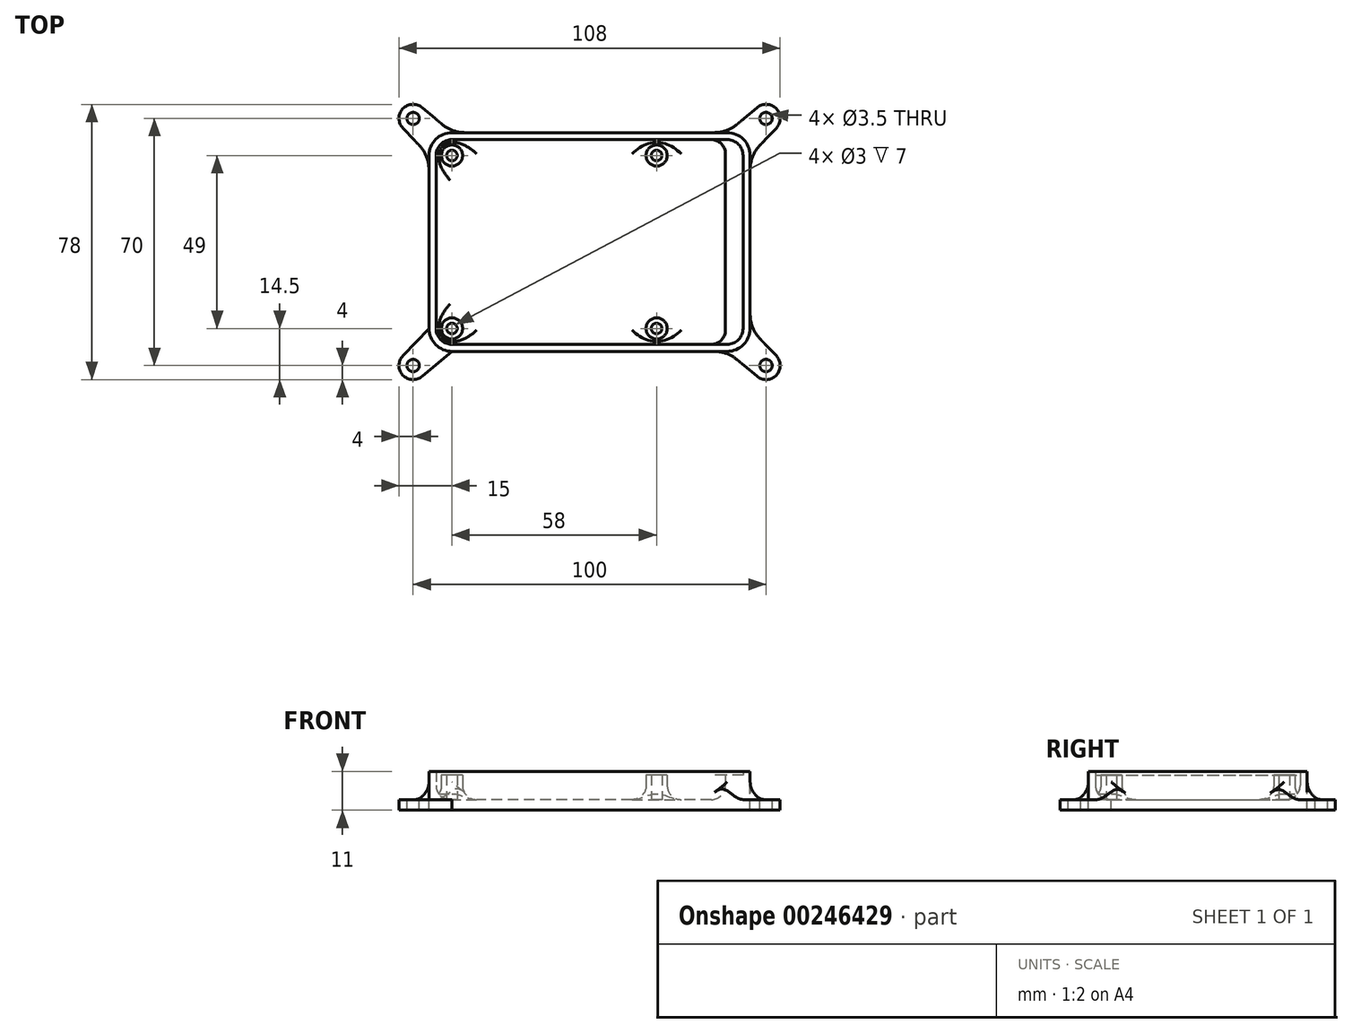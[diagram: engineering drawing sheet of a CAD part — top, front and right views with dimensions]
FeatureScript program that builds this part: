
annotation { "Feature Type Name" : "Feature", "Feature Type Description" : "" }
export const myFeature = defineFeature(function(context is Context, id is Id, definition is map)
    precondition{}
    {
        {
            var Q0;
            Q0=qCreatedBy(makeId("Top.planeOp"),FACE);
            var sketch = newSketch(context, id + "F0", { "sketchPlane" : qUnion([Q0])});
            skLineSegment(sketch, "E0.bottom", {"start": v(3.5, 0) * mm, "end": v(81.5, 0) * mm});
            skLineSegment(sketch, "E0.top", {"start": v(3.5, 56) * mm, "end": v(81.5, 56) * mm});
            skLineSegment(sketch, "E0.left", {"start": v(0, 3.5) * mm, "end": v(0, 52.5) * mm});
            skLineSegment(sketch, "E0.right", {"start": v(85, 3.5) * mm, "end": v(85, 52.5) * mm});
            skPoint(sketch, "E1.visualSharp", {"position": v(0, 56) * mm});
            skArc(sketch, "E1.filletArc", {"start": v(3.5, 56) * mm, "mid": v(1.03, 54.97) * mm, "end": v(0, 52.5) * mm});
            skPoint(sketch, "E2.visualSharp", {"position": v(85, 56) * mm});
            skArc(sketch, "E2.filletArc", {"start": v(85, 52.5) * mm, "mid": v(83.97, 54.97) * mm, "end": v(81.5, 56) * mm});
            skPoint(sketch, "E3.visualSharp", {"position": v(85, 0) * mm});
            skArc(sketch, "E3.filletArc", {"start": v(81.5, 0) * mm, "mid": v(83.97, 1.03) * mm, "end": v(85, 3.5) * mm});
            skPoint(sketch, "E4.visualSharp", {"position": v(0, 0) * mm});
            skArc(sketch, "E4.filletArc", {"start": v(0, 3.5) * mm, "mid": v(1.03, 1.03) * mm, "end": v(3.5, 0) * mm});
            skSolve(sketch);
        }
        {
            var Q0;
            Q0=makeQuery(id+"F0.imprint","IMPRINT",FACE,{"disambiguationData":[TD([[makeQuery(id+"F0.imprint","IMPRINT",EDGE,{"derivedFrom":sQuery(id+"F0.wireOp",EDGE,"E0.bottom")}),1.0]])]});
            var sketch = newSketch(context, id + "F1", { "sketchPlane" : qUnion([Q0])});
            skLineSegment(sketch, "E5.0.0", {"start": v(81.5, 56) * mm, "end": v(3.5, 56) * mm});
            skArc(sketch, "E5.0.1", {"start": v(3.5, 56) * mm, "mid": v(1.03, 54.97) * mm, "end": v(0, 52.5) * mm});
            skLineSegment(sketch, "E5.0.2", {"start": v(0, 52.5) * mm, "end": v(0, 3.5) * mm});
            skArc(sketch, "E5.0.3", {"start": v(0, 3.5) * mm, "mid": v(1.03, 1.03) * mm, "end": v(3.5, 0) * mm});
            skLineSegment(sketch, "E5.0.4", {"start": v(3.5, 0) * mm, "end": v(81.5, 0) * mm});
            skArc(sketch, "E5.0.5", {"start": v(81.5, 0) * mm, "mid": v(83.97, 1.03) * mm, "end": v(85, 3.5) * mm});
            skLineSegment(sketch, "E5.0.6", {"start": v(85, 3.5) * mm, "end": v(85, 52.5) * mm});
            skArc(sketch, "E5.0.7", {"start": v(85, 52.5) * mm, "mid": v(83.97, 54.97) * mm, "end": v(81.5, 56) * mm});
            skLineSegment(sketch, "E6.bottom", {"start": v(81.5, -1) * mm, "end": v(3.5, -1) * mm});
            skLineSegment(sketch, "E6.top", {"start": v(81.5, 57) * mm, "end": v(3.5, 57) * mm});
            skLineSegment(sketch, "E6.left", {"start": v(86, 3.5) * mm, "end": v(86, 52.5) * mm});
            skLineSegment(sketch, "E6.right", {"start": v(-1, 3.5) * mm, "end": v(-1, 52.5) * mm});
            skPoint(sketch, "E6.middle", {"position": v(42.5, 28) * mm});
            skPoint(sketch, "E6.middle.positionSnap0", {"position": v(0, 28) * mm});
            skPoint(sketch, "E6.middle.positionSnap1", {"position": v(42.5, 56) * mm});
            skPoint(sketch, "E6.centerSnap0", {"position": v(0, 28) * mm});
            skPoint(sketch, "E6.centerSnap1", {"position": v(42.5, 56) * mm});
            skPoint(sketch, "E7.visualSharp", {"position": v(-1, 57) * mm});
            skArc(sketch, "E7.filletArc", {"start": v(3.5, 57) * mm, "mid": v(0.32, 55.68) * mm, "end": v(-1, 52.5) * mm});
            skPoint(sketch, "E8.visualSharp", {"position": v(86, 57) * mm});
            skArc(sketch, "E8.filletArc", {"start": v(86, 52.5) * mm, "mid": v(84.68, 55.68) * mm, "end": v(81.5, 57) * mm});
            skPoint(sketch, "E9.visualSharp", {"position": v(86, -1) * mm});
            skArc(sketch, "E9.filletArc", {"start": v(81.5, -1) * mm, "mid": v(84.68, 0.32) * mm, "end": v(86, 3.5) * mm});
            skPoint(sketch, "E10.visualSharp", {"position": v(-1, -1) * mm});
            skArc(sketch, "E10.filletArc", {"start": v(-1, 3.5) * mm, "mid": v(0.32, 0.32) * mm, "end": v(3.5, -1) * mm});
            skLineSegment(sketch, "E11.bottom", {"start": v(81.5, -3) * mm, "end": v(3.5, -3) * mm});
            skLineSegment(sketch, "E11.top", {"start": v(81.5, 59) * mm, "end": v(3.5, 59) * mm});
            skLineSegment(sketch, "E11.left", {"start": v(88, 3.5) * mm, "end": v(88, 52.5) * mm});
            skLineSegment(sketch, "E11.right", {"start": v(-3, 3.5) * mm, "end": v(-3, 52.5) * mm});
            skPoint(sketch, "E12.visualSharp", {"position": v(-3, -3) * mm});
            skArc(sketch, "E12.filletArc", {"start": v(-3, 3.5) * mm, "mid": v(-1.1, -1.1) * mm, "end": v(3.5, -3) * mm});
            skPoint(sketch, "E13.visualSharp", {"position": v(-3, 59) * mm});
            skArc(sketch, "E13.filletArc", {"start": v(3.5, 59) * mm, "mid": v(-1.1, 57.1) * mm, "end": v(-3, 52.5) * mm});
            skPoint(sketch, "E14.visualSharp", {"position": v(88, 59) * mm});
            skArc(sketch, "E14.filletArc", {"start": v(88, 52.5) * mm, "mid": v(86.1, 57.1) * mm, "end": v(81.5, 59) * mm});
            skPoint(sketch, "E15.visualSharp", {"position": v(88, -3) * mm});
            skArc(sketch, "E15.filletArc", {"start": v(81.5, -3) * mm, "mid": v(86.1, -1.1) * mm, "end": v(88, 3.5) * mm});
            skPoint(sketch, "E16", {"position": v(-7.5, 63) * mm});
            skPoint(sketch, "E17", {"position": v(92.5, 63) * mm});
            skPoint(sketch, "E18", {"position": v(-7.5, -7) * mm});
            skPoint(sketch, "E19", {"position": v(92.5, -7) * mm});
            skCircle(sketch, "E20", {"center": v(-7.5, 63) * mm, "radius": 1.75 * mm});
            skCircle(sketch, "E21", {"center": v(92.5, 63) * mm, "radius": 1.75 * mm});
            skCircle(sketch, "E22", {"center": v(92.5, -7) * mm, "radius": 1.75 * mm});
            skCircle(sketch, "E23", {"center": v(-7.5, -7) * mm, "radius": 1.75 * mm});
            skCircle(sketch, "E24", {"center": v(92.5, 63) * mm, "radius": 4 * mm});
            skCircle(sketch, "E25", {"center": v(92.5, -7) * mm, "radius": 4 * mm});
            skCircle(sketch, "E26", {"center": v(-7.5, -7) * mm, "radius": 4 * mm});
            skCircle(sketch, "E27", {"center": v(-7.5, 63) * mm, "radius": 4 * mm});
            skLineSegment(sketch, "E28", {"start": v(-3, 52.5) * mm, "end": v(-10.4, 60.24) * mm});
            skLineSegment(sketch, "E29", {"start": v(3.5, 59) * mm, "end": v(-4.93, 66.07) * mm});
            skLineSegment(sketch, "E30", {"start": v(3.5, -3) * mm, "end": v(-4.93, -10.07) * mm});
            skLineSegment(sketch, "E31", {"start": v(-3, 3.5) * mm, "end": v(-10.4, -4.24) * mm});
            skLineSegment(sketch, "E32", {"start": v(88, 3.5) * mm, "end": v(95.4, -4.24) * mm});
            skLineSegment(sketch, "E33", {"start": v(81.5, -3) * mm, "end": v(89.93, -10.07) * mm});
            skLineSegment(sketch, "E34", {"start": v(81.5, 59) * mm, "end": v(89.93, 66.07) * mm});
            skLineSegment(sketch, "E35", {"start": v(88, 52.5) * mm, "end": v(95.4, 60.24) * mm});
            skSolve(sketch);
        }
        {
            var Q0;
            Q0=makeQuery(id+"F1.imprint","IMPRINT",FACE,{"disambiguationData":[TD([[makeQuery(id+"F1.imprint","IMPRINT",EDGE,{"derivedFrom":sQuery(id+"F1.wireOp",EDGE,"E5.0.0")}),-1.0]])]});
            var Q1;
            Q1=makeQuery(id+"F1.imprint","IMPRINT",FACE,{"disambiguationData":[TD([[makeQuery(id+"F1.imprint","IMPRINT",EDGE,{"derivedFrom":sQuery(id+"F1.wireOp",EDGE,"E5.0.0")}),1.0]])]});
            var Q2;
            Q2=makeQuery(id+"F1.imprint","IMPRINT",FACE,{"disambiguationData":[TD([[makeQuery(id+"F1.imprint","IMPRINT",EDGE,{"derivedFrom":sQuery(id+"F1.wireOp",EDGE,"E6.bottom")}),1.0]])]});
            var Q3;
            Q3=makeQuery(id+"F1.imprint","IMPRINT",FACE,{"disambiguationData":[TD([[makeQuery(id+"F1.imprint","IMPRINT",EDGE,{"derivedFrom":sQuery(id+"F1.wireOp",EDGE,"E13.filletArc")}),-1.0]])]});
            var Q4;
            Q4=makeQuery(id+"F1.imprint","IMPRINT",FACE,{"disambiguationData":[TD([[makeQuery(id+"F1.imprint","IMPRINT",EDGE,{"derivedFrom":sQuery(id+"F1.wireOp",EDGE,"E20")}),-1.0]])]});
            var Q5;
            Q5=makeQuery(id+"F1.imprint","IMPRINT",FACE,{"disambiguationData":[TD([[makeQuery(id+"F1.imprint","IMPRINT",EDGE,{"derivedFrom":sQuery(id+"F1.wireOp",EDGE,"E14.filletArc")}),-1.0]])]});
            var Q6;
            Q6=makeQuery(id+"F1.imprint","IMPRINT",FACE,{"disambiguationData":[TD([[makeQuery(id+"F1.imprint","IMPRINT",EDGE,{"derivedFrom":sQuery(id+"F1.wireOp",EDGE,"E21")}),-1.0]])]});
            var Q7;
            Q7=makeQuery(id+"F1.imprint","IMPRINT",FACE,{"disambiguationData":[TD([[makeQuery(id+"F1.imprint","IMPRINT",EDGE,{"derivedFrom":sQuery(id+"F1.wireOp",EDGE,"E15.filletArc")}),-1.0]])]});
            var Q8;
            Q8=makeQuery(id+"F1.imprint","IMPRINT",FACE,{"disambiguationData":[TD([[makeQuery(id+"F1.imprint","IMPRINT",EDGE,{"derivedFrom":sQuery(id+"F1.wireOp",EDGE,"E22")}),-1.0]])]});
            var Q9;
            Q9=makeQuery(id+"F1.imprint","IMPRINT",FACE,{"disambiguationData":[TD([[makeQuery(id+"F1.imprint","IMPRINT",EDGE,{"derivedFrom":sQuery(id+"F1.wireOp",EDGE,"E12.filletArc")}),-1.0]])]});
            var Q10;
            Q10=makeQuery(id+"F1.imprint","IMPRINT",FACE,{"disambiguationData":[TD([[makeQuery(id+"F1.imprint","IMPRINT",EDGE,{"derivedFrom":sQuery(id+"F1.wireOp",EDGE,"E23")}),-1.0]])]});
            extrude(context, id + "F2", {"entities" : qUnion([Q0, Q1, Q2, Q3, Q4, Q5, Q6, Q7, Q8, Q9, Q10]), "oppositeDirection" : true, "depth" : 3 * mm});
        }
        {
            var Q0;
            Q0=makeQuery(id+"F1.imprint","IMPRINT",FACE,{"disambiguationData":[TD([[makeQuery(id+"F1.imprint","IMPRINT",EDGE,{"derivedFrom":sQuery(id+"F1.wireOp",EDGE,"E6.bottom")}),1.0]])]});
            extrude(context, id + "F3", {"entities" : qUnion([Q0]), "operationType" : NewBodyOperationType.ADD, "depth" : 8 * mm});
        }
        {
            var Q0;
            Q0=makeQuery(id+"F1.imprint","IMPRINT",FACE,{"disambiguationData":[TD([[makeQuery(id+"F1.imprint","IMPRINT",EDGE,{"derivedFrom":sQuery(id+"F1.wireOp",EDGE,"E5.0.0")}),-1.0]])]});
            var sketch = newSketch(context, id + "F4", { "sketchPlane" : qUnion([Q0])});
            skCircle(sketch, "E36", {"center": v(3.5, 52.5) * mm, "radius": 1.5 * mm});
            skCircle(sketch, "E37", {"center": v(61.5, 52.5) * mm, "radius": 1.5 * mm});
            skCircle(sketch, "E38", {"center": v(3.5, 3.5) * mm, "radius": 1.5 * mm});
            skCircle(sketch, "E39", {"center": v(61.5, 3.5) * mm, "radius": 1.5 * mm});
            skCircle(sketch, "E40", {"center": v(3.5, 52.5) * mm, "radius": 3 * mm});
            skCircle(sketch, "E41", {"center": v(61.5, 52.5) * mm, "radius": 3 * mm});
            skCircle(sketch, "E42", {"center": v(3.5, 3.5) * mm, "radius": 3 * mm});
            skCircle(sketch, "E43", {"center": v(61.5, 3.5) * mm, "radius": 3 * mm});
            skLineSegment(sketch, "E44.0", {"start": v(86, 3.5) * mm, "end": v(86, 52.5) * mm});
            skLineSegment(sketch, "E45.0", {"start": v(81.5, -3) * mm, "end": v(3.5, -3) * mm});
            skLineSegment(sketch, "E46.0", {"start": v(81.5, 59) * mm, "end": v(3.5, 59) * mm});
            skArc(sketch, "E47.0", {"start": v(88, 52.5) * mm, "mid": v(86.1, 57.1) * mm, "end": v(81.5, 59) * mm});
            skLineSegment(sketch, "E48.0", {"start": v(88, 3.5) * mm, "end": v(88, 52.5) * mm});
            skArc(sketch, "E49.0", {"start": v(81.5, -3) * mm, "mid": v(86.1, -1.1) * mm, "end": v(88, 3.5) * mm});
            skLineSegment(sketch, "E50", {"start": v(81, -3) * mm, "end": v(81, 59) * mm});
            skSolve(sketch);
        }
        {
            var Q0;
            Q0=makeQuery(id+"F4.imprint","IMPRINT",FACE,{"disambiguationData":[TD([[makeQuery(id+"F4.imprint","IMPRINT",EDGE,{"derivedFrom":sQuery(id+"F4.wireOp",EDGE,"E36")}),-1.0]])]});
            var Q1;
            Q1=makeQuery(id+"F4.imprint","IMPRINT",FACE,{"disambiguationData":[TD([[makeQuery(id+"F4.imprint","IMPRINT",EDGE,{"derivedFrom":sQuery(id+"F4.wireOp",EDGE,"E37")}),-1.0]])]});
            var Q2;
            Q2=makeQuery(id+"F4.imprint","IMPRINT",FACE,{"disambiguationData":[TD([[makeQuery(id+"F4.imprint","IMPRINT",EDGE,{"derivedFrom":sQuery(id+"F4.wireOp",EDGE,"E39")}),-1.0]])]});
            var Q3;
            Q3=makeQuery(id+"F4.imprint","IMPRINT",FACE,{"disambiguationData":[TD([[makeQuery(id+"F4.imprint","IMPRINT",EDGE,{"derivedFrom":sQuery(id+"F4.wireOp",EDGE,"E38")}),-1.0]])]});
            var Q4;
            {var subQ1=makeQuery(id+"F1.imprint","IMPRINT",EDGE,{"derivedFrom":sQuery(id+"F1.wireOp",EDGE,"E5.0.5")});Q4=makeQuery(id+"F4.imprint","IMPRINT",FACE,{"disambiguationData":[TD([[makeQuery(id+"F4.imprint","IMPRINT",EDGE,{"derivedFrom":subQ1}),1.0]])]});}
            var Q5;
            {var subQ1=sQuery(id+"F4.wireOp",EDGE,"E47.0");Q5=makeQuery(id+"F4.imprint","IMPRINT",FACE,{"disambiguationData":[TD([[makeQuery(id+"F4.imprint","IMPRINT",EDGE,{"derivedFrom":subQ1}),1.0]])]});}
            extrude(context, id + "F5", {"entities" : qUnion([Q0, Q1, Q2, Q3, Q4, Q5]), "operationType" : NewBodyOperationType.ADD, "depth" : 7 * mm});
        }
        {
            var Q0;
            Q0=makeQuery(id+"F5.boolean.opBoolean","SPLIT",FACE,{"disambiguationData":[TD([makeQuery(id+"F3.opExtrude","SWEPT_FACE",FACE,{"disambiguationData":[OSD([sQuery(id+"F1.wireOp",EDGE,"E6.bottom")])]})])],"derivedFrom":makeQuery(id+"F2.opExtrude","CAP_FACE",FACE,{"disambiguationData":[OSD([sQuery(id+"F1.wireOp",EDGE,"E11.bottom"),sQuery(id+"F1.wireOp",EDGE,"E11.top"),sQuery(id+"F1.wireOp",EDGE,"E11.left"),sQuery(id+"F1.wireOp",EDGE,"E11.right"),sQuery(id+"F1.wireOp",EDGE,"E12.filletArc"),sQuery(id+"F1.wireOp",EDGE,"E13.filletArc"),sQuery(id+"F1.wireOp",EDGE,"E14.filletArc"),sQuery(id+"F1.wireOp",EDGE,"E15.filletArc")])],"isStart":true})});
            var Q1;
            Q1=makeQuery(id+"F5.boolean.opBoolean","INTERSECT",EDGE,{"derivedFrom":[makeQuery(id+"F3.opExtrude","SWEPT_FACE",FACE,{"disambiguationData":[OSD([sQuery(id+"F1.wireOp",EDGE,"E6.top")])]}),makeQuery(id+"F5.opExtrude","SWEPT_FACE",FACE,{"disambiguationData":[OSD([sQuery(id+"F4.wireOp",EDGE,"E50")])]})]});
            var Q2;
            Q2=makeQuery(id+"F5.boolean.opBoolean","INTERSECT",EDGE,{"derivedFrom":[makeQuery(id+"F3.opExtrude","SWEPT_FACE",FACE,{"disambiguationData":[OSD([sQuery(id+"F1.wireOp",EDGE,"E6.bottom")])]}),makeQuery(id+"F5.opExtrude","SWEPT_FACE",FACE,{"disambiguationData":[OSD([sQuery(id+"F4.wireOp",EDGE,"E50")])]})]});
            fillet(context, id + "F6", {"entities" : qUnion([Q0, Q1, Q2]), "radius" : 4 * mm, "tangentPropagation" : true, "allowEdgeOverflow" : false});
        }
        {
            var Q0;
            Q0=makeQuery(id+"F3.opExtrude","CAP_EDGE",EDGE,{"disambiguationData":[OSD([sQuery(id+"F1.wireOp",EDGE,"E15.filletArc")])],"isStart":true});
            var Q1;
            Q1=makeQuery(id+"F3.opExtrude","CAP_EDGE",EDGE,{"disambiguationData":[OSD([sQuery(id+"F1.wireOp",EDGE,"E12.filletArc")])],"isStart":true});
            var Q2;
            Q2=makeQuery(id+"F3.opExtrude","CAP_EDGE",EDGE,{"disambiguationData":[OSD([sQuery(id+"F1.wireOp",EDGE,"E14.filletArc")])],"isStart":true});
            var Q3;
            Q3=makeQuery(id+"F3.opExtrude","CAP_EDGE",EDGE,{"disambiguationData":[OSD([sQuery(id+"F1.wireOp",EDGE,"E13.filletArc")])],"isStart":true});
            fillet(context, id + "F7", {"entities" : qUnion([Q0, Q1, Q2, Q3]), "radius" : 5 * mm, "tangentPropagation" : true, "allowEdgeOverflow" : false});
        }
        {
            var Q0;
            {var subQ0=sQuery(id+"F1.wireOp",EDGE,"E29");var subQ1=sQuery(id+"F1.wireOp",EDGE,"E13.filletArc");var subQ2=sQuery(id+"F1.wireOp",EDGE,"E11.top");Q0=makeQuery(id+"F7.opFillet","MERGE",EDGE,{"derivedFrom":[makeQuery(id+"F2.opExtrude","SWEPT_EDGE",EDGE,{"disambiguationData":[OSD([subQ2,subQ1,subQ0])]}),makeQuery(id+"F3.opExtrude","SWEPT_EDGE",EDGE,{"disambiguationData":[OSD([subQ2,subQ1,subQ0])]})]});}
            var Q1;
            {var subQ0=sQuery(id+"F1.wireOp",EDGE,"E34");var subQ1=sQuery(id+"F1.wireOp",EDGE,"E14.filletArc");var subQ2=sQuery(id+"F1.wireOp",EDGE,"E11.top");Q1=makeQuery(id+"F7.opFillet","MERGE",EDGE,{"derivedFrom":[makeQuery(id+"F2.opExtrude","SWEPT_EDGE",EDGE,{"disambiguationData":[OSD([subQ2,subQ1,subQ0])]}),makeQuery(id+"F3.opExtrude","SWEPT_EDGE",EDGE,{"disambiguationData":[OSD([subQ2,subQ1,subQ0])]})]});}
            var Q2;
            {var subQ0=sQuery(id+"F1.wireOp",EDGE,"E35");var subQ1=sQuery(id+"F1.wireOp",EDGE,"E14.filletArc");var subQ2=sQuery(id+"F1.wireOp",EDGE,"E11.left");Q2=makeQuery(id+"F7.opFillet","MERGE",EDGE,{"derivedFrom":[makeQuery(id+"F2.opExtrude","SWEPT_EDGE",EDGE,{"disambiguationData":[OSD([subQ2,subQ1,subQ0])]}),makeQuery(id+"F3.opExtrude","SWEPT_EDGE",EDGE,{"disambiguationData":[OSD([subQ2,subQ1,subQ0])]})]});}
            var Q3;
            {var subQ0=sQuery(id+"F1.wireOp",EDGE,"E32");var subQ1=sQuery(id+"F1.wireOp",EDGE,"E15.filletArc");var subQ2=sQuery(id+"F1.wireOp",EDGE,"E11.left");Q3=makeQuery(id+"F7.opFillet","MERGE",EDGE,{"derivedFrom":[makeQuery(id+"F2.opExtrude","SWEPT_EDGE",EDGE,{"disambiguationData":[OSD([subQ2,subQ1,subQ0])]}),makeQuery(id+"F3.opExtrude","SWEPT_EDGE",EDGE,{"disambiguationData":[OSD([subQ2,subQ1,subQ0])]})]});}
            var Q4;
            {var subQ0=sQuery(id+"F1.wireOp",EDGE,"E33");var subQ1=sQuery(id+"F1.wireOp",EDGE,"E15.filletArc");var subQ2=sQuery(id+"F1.wireOp",EDGE,"E11.bottom");Q4=makeQuery(id+"F7.opFillet","MERGE",EDGE,{"derivedFrom":[makeQuery(id+"F2.opExtrude","SWEPT_EDGE",EDGE,{"disambiguationData":[OSD([subQ2,subQ1,subQ0])]}),makeQuery(id+"F3.opExtrude","SWEPT_EDGE",EDGE,{"disambiguationData":[OSD([subQ2,subQ1,subQ0])]})]});}
            var Q5;
            {var subQ0=sQuery(id+"F1.wireOp",EDGE,"E30");var subQ1=sQuery(id+"F1.wireOp",EDGE,"E12.filletArc");var subQ2=sQuery(id+"F1.wireOp",EDGE,"E11.bottom");Q5=makeQuery(id+"F7.opFillet","MERGE",EDGE,{"derivedFrom":[makeQuery(id+"F2.opExtrude","SWEPT_EDGE",EDGE,{"disambiguationData":[OSD([subQ2,subQ1,subQ0])]}),makeQuery(id+"F3.opExtrude","SWEPT_EDGE",EDGE,{"disambiguationData":[OSD([subQ2,subQ1,subQ0])]})]});}
            var Q6;
            {var subQ0=sQuery(id+"F1.wireOp",EDGE,"E28");var subQ1=sQuery(id+"F1.wireOp",EDGE,"E13.filletArc");var subQ2=sQuery(id+"F1.wireOp",EDGE,"E11.right");Q6=makeQuery(id+"F7.opFillet","MERGE",EDGE,{"derivedFrom":[makeQuery(id+"F2.opExtrude","SWEPT_EDGE",EDGE,{"disambiguationData":[OSD([subQ2,subQ1,subQ0])]}),makeQuery(id+"F3.opExtrude","SWEPT_EDGE",EDGE,{"disambiguationData":[OSD([subQ2,subQ1,subQ0])]})]});}
            var Q7;
            {var subQ0=sQuery(id+"F1.wireOp",EDGE,"E31");var subQ1=sQuery(id+"F1.wireOp",EDGE,"E12.filletArc");var subQ2=sQuery(id+"F1.wireOp",EDGE,"E11.right");Q7=makeQuery(id+"F7.opFillet","MERGE",EDGE,{"derivedFrom":[makeQuery(id+"F2.opExtrude","SWEPT_EDGE",EDGE,{"disambiguationData":[OSD([subQ2,subQ1,subQ0])]}),makeQuery(id+"F3.opExtrude","SWEPT_EDGE",EDGE,{"disambiguationData":[OSD([subQ2,subQ1,subQ0])]})]});}
            fillet(context, id + "F8", {"entities" : qUnion([Q0, Q1, Q2, Q3, Q4, Q5, Q6, Q7]), "radius" : 10 * mm, "tangentPropagation" : true, "allowEdgeOverflow" : false});
        }
    });
